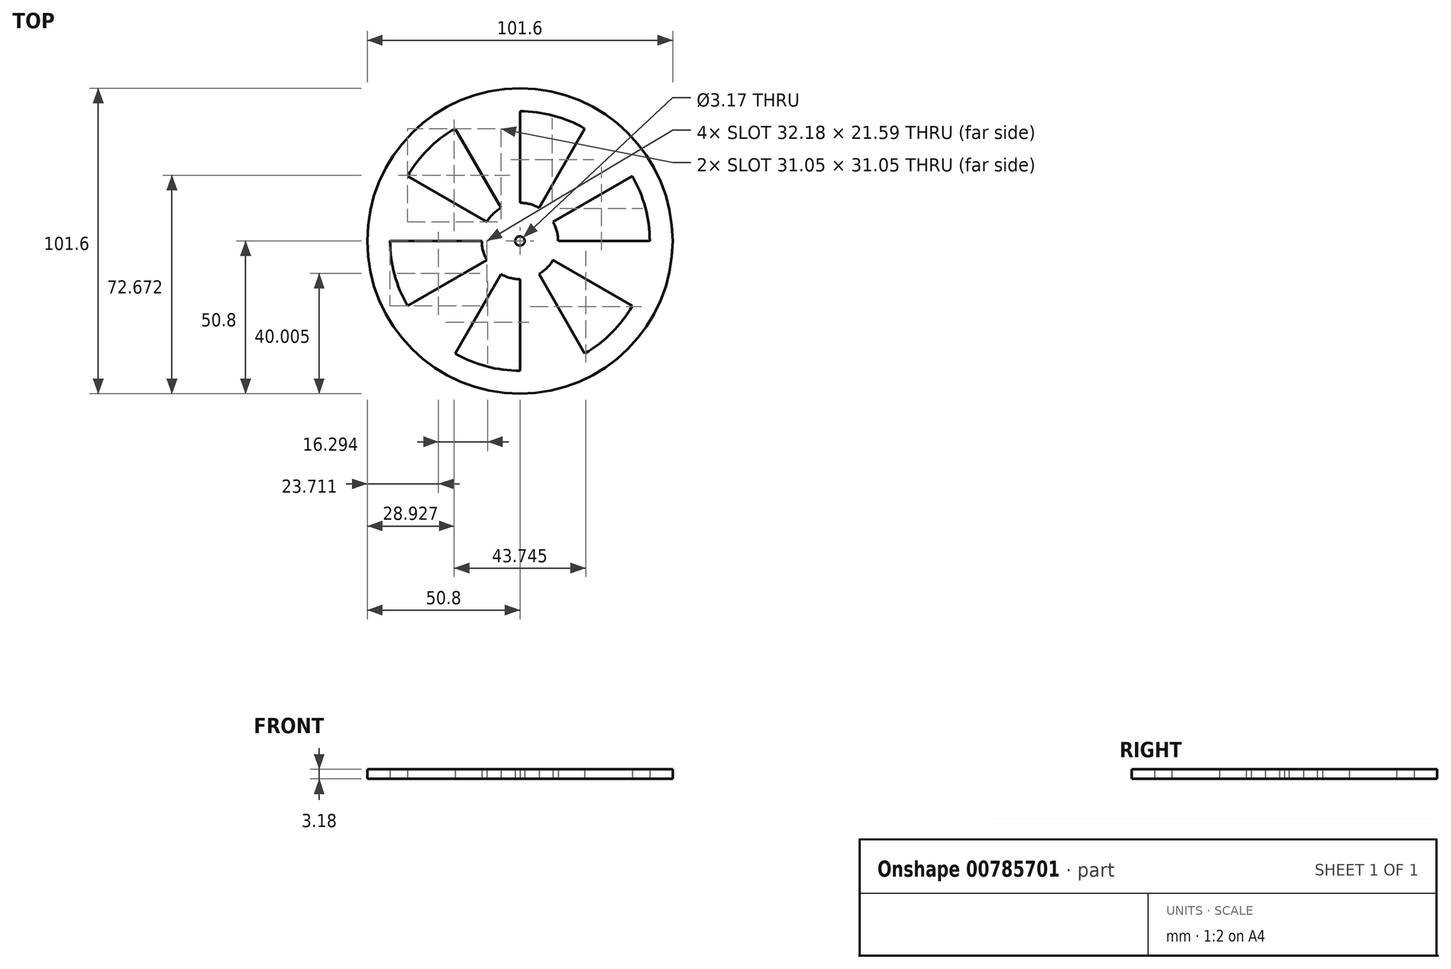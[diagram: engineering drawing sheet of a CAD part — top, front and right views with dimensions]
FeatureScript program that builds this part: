
annotation { "Feature Type Name" : "Feature", "Feature Type Description" : "" }
export const myFeature = defineFeature(function(context is Context, id is Id, definition is map)
    precondition{}
    {
        {
            var Q0;
            Q0=qCreatedBy(makeId("Top.planeOp"),FACE);
            var sketch = newSketch(context, id + "F0", { "sketchPlane" : qUnion([Q0])});
            skCircle(sketch, "E0", {"center": v(0, 0) * mm, "radius": 50.8 * mm});
            skArc(sketch, "E1", {"start": v(-21.59, 37.4) * mm, "mid": v(-30.53, 30.53) * mm, "end": v(-37.4, 21.6) * mm});
            skArc(sketch, "E2", {"start": v(-6.35, 11) * mm, "mid": v(-8.98, 8.98) * mm, "end": v(-11, 6.35) * mm});
            skLineSegment(sketch, "E3", {"start": v(0, 43.18) * mm, "end": v(0, 12.7) * mm});
            skLineSegment(sketch, "E4", {"start": v(37.4, -21.59) * mm, "end": v(11, -6.35) * mm});
            skLineSegment(sketch, "E5", {"start": v(6.35, 11) * mm, "end": v(21.59, 37.4) * mm});
            skLineSegment(sketch, "E6", {"start": v(11, 6.35) * mm, "end": v(37.4, 21.6) * mm});
            skPoint(sketch, "E7.endSnap0", {"position": v(-10.8, -18.7) * mm});
            skPoint(sketch, "E8.orphan", {"position": v(-43.18, 0) * mm});
            skPoint(sketch, "E9.orphan", {"position": v(-38.92, -18.7) * mm});
            skPoint(sketch, "E10.orphan", {"position": v(-21.59, -37.4) * mm});
            skLineSegment(sketch, "E11", {"start": v(6.35, -11) * mm, "end": v(21.6, -37.4) * mm});
            skLineSegment(sketch, "E12.MirrorCS", {"start": v(-6.35, 11) * mm, "end": v(-21.59, 37.4) * mm});
            skLineSegment(sketch, "E13.MirrorCS", {"start": v(-11, 6.35) * mm, "end": v(-37.4, 21.6) * mm});
            skLineSegment(sketch, "E14.MirrorCS", {"start": v(12.7, 0) * mm, "end": v(-43.18, 0) * mm});
            skLineSegment(sketch, "E15.MirrorCS", {"start": v(-37.4, -21.59) * mm, "end": v(-11, -6.35) * mm});
            skLineSegment(sketch, "E16.MirrorCS", {"start": v(-6.35, -11) * mm, "end": v(-21.6, -37.4) * mm});
            skLineSegment(sketch, "E17.trimOffspring", {"start": v(0, -12.7) * mm, "end": v(0, -43.18) * mm});
            skLineSegment(sketch, "E18.trimOffspring", {"start": v(12.7, 0) * mm, "end": v(43.18, 0) * mm});
            skPoint(sketch, "E19.end.orphan", {"position": v(-6.35, -11) * mm});
            skPoint(sketch, "E20.start.orphan", {"position": v(-12.7, 0) * mm});
            skCircle(sketch, "E21", {"center": v(0, 0) * mm, "radius": 1.59 * mm});
            skArc(sketch, "E22.trimOffspring", {"start": v(6.35, 11) * mm, "mid": v(3.29, 12.27) * mm, "end": v(0, 12.7) * mm});
            skArc(sketch, "E23.trimOffspring", {"start": v(21.59, 37.4) * mm, "mid": v(11.18, 41.7) * mm, "end": v(0, 43.18) * mm});
            skArc(sketch, "E24.trimOffspring", {"start": v(12.7, 0) * mm, "mid": v(12.27, 3.29) * mm, "end": v(11, 6.35) * mm});
            skArc(sketch, "E25.trimOffspring", {"start": v(43.18, 0) * mm, "mid": v(41.7, 11.18) * mm, "end": v(37.4, 21.6) * mm});
            skArc(sketch, "E26.trimOffspring", {"start": v(6.35, -11) * mm, "mid": v(8.98, -8.98) * mm, "end": v(11, -6.35) * mm});
            skArc(sketch, "E27.trimOffspring", {"start": v(21.6, -37.4) * mm, "mid": v(30.53, -30.53) * mm, "end": v(37.4, -21.59) * mm});
            skArc(sketch, "E28.trimOffspring", {"start": v(-6.35, -11) * mm, "mid": v(-3.29, -12.27) * mm, "end": v(0, -12.7) * mm});
            skArc(sketch, "E29.trimOffspring", {"start": v(-21.59, -37.4) * mm, "mid": v(-11.18, -41.7) * mm, "end": v(0, -43.18) * mm});
            skArc(sketch, "E30.trimOffspring", {"start": v(-12.7, 0) * mm, "mid": v(-12.27, -3.29) * mm, "end": v(-11, -6.35) * mm});
            skArc(sketch, "E31.trimOffspring", {"start": v(-43.18, 0) * mm, "mid": v(-41.7, -11.18) * mm, "end": v(-37.4, -21.59) * mm});
            skSolve(sketch);
        }
        {
            var Q0;
            Q0=makeQuery(id+"F0.imprint","IMPRINT",FACE,{"disambiguationData":[TD([[makeQuery(id+"F0.imprint","IMPRINT",EDGE,{"derivedFrom":sQuery(id+"F0.wireOp",EDGE,"E0")}),1.0]])]});
            extrude(context, id + "F1", {"entities" : qUnion([Q0]), "depth" : 3.17 * mm, "offsetDistance" : 25.4 * mm});
        }
    });
